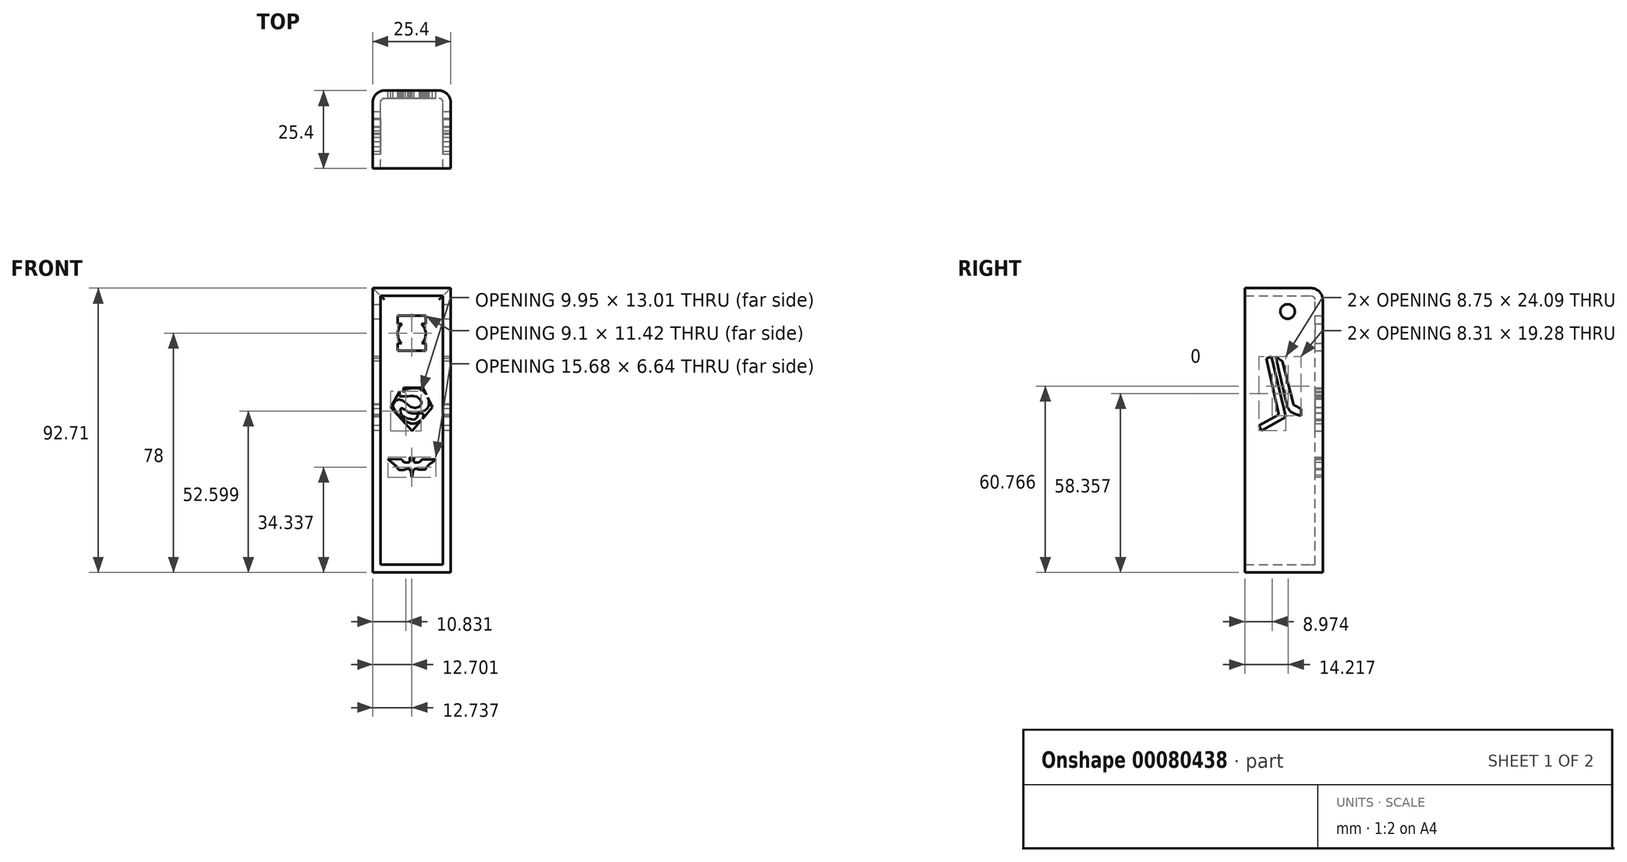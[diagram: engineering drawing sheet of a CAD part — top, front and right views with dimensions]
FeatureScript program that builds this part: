
annotation { "Feature Type Name" : "Feature", "Feature Type Description" : "" }
export const myFeature = defineFeature(function(context is Context, id is Id, definition is map)
    precondition{}
    {
        {
            var Q0;
            Q0=qCreatedBy(makeId("Front.planeOp"),FACE);
            var sketch = newSketch(context, id + "F0", { "sketchPlane" : qUnion([Q0])});
            skLineSegment(sketch, "E0.bottom", {"start": v(-54.67, 58.84) * mm, "end": v(-29.27, 58.84) * mm});
            skLineSegment(sketch, "E0.top", {"start": v(-54.67, -33.87) * mm, "end": v(-29.27, -33.87) * mm});
            skLineSegment(sketch, "E0.left", {"start": v(-54.67, 58.84) * mm, "end": v(-54.67, -33.87) * mm});
            skLineSegment(sketch, "E0.right", {"start": v(-29.27, 58.84) * mm, "end": v(-29.27, -33.87) * mm});
            skSolve(sketch);
        }
        {
            var Q0;
            Q0=makeQuery(id+"F0.imprint","IMPRINT",FACE,{"disambiguationData":[TD([[makeQuery(id+"F0.imprint","IMPRINT",EDGE,{"derivedFrom":sQuery(id+"F0.wireOp",EDGE,"E0.bottom")}),-1.0]])]});
            extrude(context, id + "F1", {"entities" : qUnion([Q0]), "depth" : 25.4 * mm});
        }
        {
            var Q0;
            Q0=makeQuery(id+"F1.opExtrude","CAP_EDGE",EDGE,{"disambiguationData":[OSD([sQuery(id+"F0.wireOp",EDGE,"E0.bottom")])],"isStart":true});
            var Q1;
            Q1=makeQuery(id+"F1.opExtrude","CAP_EDGE",EDGE,{"disambiguationData":[OSD([sQuery(id+"F0.wireOp",EDGE,"E0.right")])],"isStart":true});
            var Q2;
            Q2=makeQuery(id+"F1.opExtrude","CAP_EDGE",EDGE,{"disambiguationData":[OSD([sQuery(id+"F0.wireOp",EDGE,"E0.left")])],"isStart":true});
            fillet(context, id + "F2", {"entities" : qUnion([Q0, Q1, Q2]), "radius" : 3.8 * mm, "tangentPropagation" : true, "allowEdgeOverflow" : false});
        }
        {
            var Q0;
            Q0=makeQuery(id+"F1.opExtrude","CAP_FACE",FACE,{"disambiguationData":[OSD([sQuery(id+"F0.wireOp",EDGE,"E0.bottom"),sQuery(id+"F0.wireOp",EDGE,"E0.top"),sQuery(id+"F0.wireOp",EDGE,"E0.left"),sQuery(id+"F0.wireOp",EDGE,"E0.right")])],"isStart":false});
            shell(context, id + "F3", {"entities" : qUnion([Q0]), "thickness" : 2.54 * mm});
        }
        {
            var Q0;
            Q0=makeQuery(id+"F1.opExtrude","SWEPT_FACE",FACE,{"disambiguationData":[OSD([sQuery(id+"F0.wireOp",EDGE,"E0.right")])]});
            var sketch = newSketch(context, id + "F4", { "sketchPlane" : qUnion([Q0])});
            skCircle(sketch, "E1", {"center": v(-11.43, 51.22) * mm, "radius": 2.37 * mm});
            skSolve(sketch);
        }
        {
            var Q0;
            Q0=makeQuery(id+"F4.imprint","IMPRINT",FACE,{"disambiguationData":[TD([[makeQuery(id+"F4.imprint","IMPRINT",EDGE,{"derivedFrom":sQuery(id+"F4.wireOp",EDGE,"E1")}),1.0]])]});
            extrude(context, id + "F5", {"entities" : qUnion([Q0]), "operationType" : NewBodyOperationType.REMOVE, "oppositeDirection" : true, "depth" : 33.9 * mm});
        }
        {
            var Q0;
            Q0=makeQuery(id+"F1.opExtrude","CAP_FACE",FACE,{"disambiguationData":[OSD([sQuery(id+"F0.wireOp",EDGE,"E0.bottom"),sQuery(id+"F0.wireOp",EDGE,"E0.top"),sQuery(id+"F0.wireOp",EDGE,"E0.left"),sQuery(id+"F0.wireOp",EDGE,"E0.right")])],"isStart":true});
            var sketch = newSketch(context, id + "F6", { "sketchPlane" : qUnion([Q0])});
            skLineSegment(sketch, "E2", {"start": v(38.24, 26.3) * mm, "end": v(45.34, 26.3) * mm});
            skLineSegment(sketch, "E3", {"start": v(45.34, 26.3) * mm, "end": v(48.82, 20) * mm});
            skLineSegment(sketch, "E4", {"start": v(48.82, 20) * mm, "end": v(41.79, 12.22) * mm});
            skLineSegment(sketch, "E5", {"start": v(38.24, 26.3) * mm, "end": v(35.18, 20) * mm});
            skLineSegment(sketch, "E6", {"start": v(35.18, 20) * mm, "end": v(41.79, 12.22) * mm});
            skPoint(sketch, "E6.endSnap0", {"position": v(41.79, 26.3) * mm});
            skLineSegment(sketch, "E7", {"start": v(45.93, 25.23) * mm, "end": v(45.93, 23.52) * mm});
            skLineSegment(sketch, "E8", {"start": v(45.93, 23.52) * mm, "end": v(43.24, 23.52) * mm});
            skLineSegment(sketch, "E9", {"start": v(43.25, 18.52) * mm, "end": v(42.79, 18.26) * mm});
            skLineSegment(sketch, "E10", {"start": v(44.01, 25.93) * mm, "end": v(44.6, 24.83) * mm});
            skLineSegment(sketch, "E11", {"start": v(44.6, 24.83) * mm, "end": v(44.6, 26.3) * mm});
            skFitSpline(sketch, "E12", {"points": [v(43.24, 23.52) * mm, v(42.18, 23.7) * mm, v(41.34, 23.73) * mm, v(39, 22.4) * mm, v(38.86, 21.23) * mm, v(39.13, 20.53) * mm, v(40.91, 19.71) * mm, v(43.9, 21.34) * mm, v(46.12, 22.6) * mm, v(48.1, 20.99) * mm, v(47.19, 18.57) * mm, v(45.7, 16.78) * mm, v(42.61, 14.78) * mm, v(40.7, 14.7) * mm, v(38.86, 15.67) * mm, v(38.23, 16.65) * mm, v(38.36, 17.92) * mm, v(39.75, 17.72) * mm, v(40.62, 16.18) * mm, v(42.98, 16.28) * mm, v(45.43, 17.74) * mm, v(45.37, 19.7) * mm, v(42.79, 18.26) * mm, v(39.33, 18.25) * mm, v(36.88, 19.7) * mm, v(36.37, 21.85) * mm, v(37.82, 24.97) * mm, v(40.4, 26.27) * mm, v(44.01, 25.93) * mm], "startDerivative": vector(-64, 34.12) * mm, "endDerivative": vector(80.29, -7.6) * mm});
            skLineSegment(sketch, "E13", {"start": v(37.92, 26.85) * mm, "end": v(45.8, 26.85) * mm});
            skLineSegment(sketch, "E14", {"start": v(45.8, 26.85) * mm, "end": v(49.52, 20.02) * mm});
            skLineSegment(sketch, "E15", {"start": v(49.52, 20.02) * mm, "end": v(41.8, 11.45) * mm});
            skLineSegment(sketch, "E16", {"start": v(37.92, 26.85) * mm, "end": v(34.6, 20.06) * mm});
            skLineSegment(sketch, "E17", {"start": v(34.6, 20.06) * mm, "end": v(41.8, 11.45) * mm});
            skLineSegment(sketch, "E18", {"start": v(34.1, 3.04) * mm, "end": v(38.67, 3.04) * mm});
            skLineSegment(sketch, "E19", {"start": v(41.97, -31.17) * mm, "end": v(41.97, -31.17) * mm});
            skPoint(sketch, "E19.startSnap0", {"position": v(41.97, 55.03) * mm});
            skLineSegment(sketch, "E20", {"start": v(37.09, 0.46) * mm, "end": v(37.51, -0.37) * mm});
            skLineSegment(sketch, "E21", {"start": v(37.51, -0.37) * mm, "end": v(39.42, -0.37) * mm});
            skLineSegment(sketch, "E22.MirrorCS", {"start": v(49.77, 3.06) * mm, "end": v(45.2, 3.05) * mm});
            skFitSpline(sketch, "E23", {"points": [v(34.1, 3.04) * mm, v(37.09, 0.46) * mm, v(37.51, -0.37) * mm], "startDerivative": vector(5.4, -4.4) * mm, "endDerivative": vector(1.96, -3.42) * mm});
            skFitSpline(sketch, "E24", {"points": [v(37.51, -0.37) * mm, v(39.42, -0.37) * mm, v(41.5, -0.78) * mm, v(41.94, -2.12) * mm], "startDerivative": vector(3.85, 0) * mm, "endDerivative": vector(-0.02, 19.13) * mm});
            skFitSpline(sketch, "E25", {"points": [v(41.94, -2.12) * mm, v(42.38, -0.78) * mm, v(44.45, -0.37) * mm, v(46.36, -0.36) * mm], "startDerivative": vector(0.02, -19.13) * mm, "endDerivative": vector(4.94, -0.06) * mm});
            skFitSpline(sketch, "E26", {"points": [v(46.36, -0.36) * mm, v(46.78, 0.47) * mm, v(49.77, 3.06) * mm], "startDerivative": vector(1.36, 2.43) * mm, "endDerivative": vector(5.4, 4.4) * mm});
            skFitSpline(sketch, "E27", {"points": [v(45.2, 3.05) * mm, v(44.74, 2.33) * mm, v(43.56, 1.98) * mm, v(42.69, 2.24) * mm, v(42.69, 3.78) * mm], "startDerivative": vector(-2.36, -3.44) * mm, "endDerivative": vector(1.09, 6.4) * mm});
            skFitSpline(sketch, "E28", {"points": [v(41.18, 3.78) * mm, v(41.18, 2.24) * mm, v(40.3, 1.98) * mm, v(39.12, 2.32) * mm, v(38.67, 3.04) * mm], "startDerivative": vector(1.09, -6.4) * mm, "endDerivative": vector(-2.36, 3.44) * mm});
            skFitSpline(sketch, "E29", {"points": [v(41.18, 3.78) * mm, v(41.59, 3.12) * mm, v(41.93, 3.12) * mm, v(42.28, 3.12) * mm, v(42.69, 3.78) * mm], "startDerivative": vector(0.92, -3.28) * mm, "endDerivative": vector(0.92, 3.28) * mm});
            skPoint(sketch, "E30", {"position": v(37.3, 0.04) * mm});
            skLineSegment(sketch, "E31", {"start": v(41.97, 49.84) * mm, "end": v(37.42, 49.84) * mm});
            skLineSegment(sketch, "E32", {"start": v(37.42, 49.84) * mm, "end": v(37.42, 47.19) * mm});
            skLineSegment(sketch, "E33", {"start": v(37.42, 47.19) * mm, "end": v(40.3, 47.19) * mm});
            skLineSegment(sketch, "E34", {"start": v(40.3, 40.84) * mm, "end": v(37.42, 40.84) * mm});
            skLineSegment(sketch, "E35", {"start": v(37.42, 40.84) * mm, "end": v(37.42, 38.42) * mm});
            skLineSegment(sketch, "E36", {"start": v(37.42, 38.42) * mm, "end": v(41.97, 38.42) * mm});
            skCircle(sketch, "E37", {"center": v(41.97, 43.92) * mm, "radius": 4.55 * mm});
            skLineSegment(sketch, "E38", {"start": v(41.97, 49.84) * mm, "end": v(41.97, 38.42) * mm});
            skLineSegment(sketch, "E39.MirrorCS", {"start": v(46.52, 49.84) * mm, "end": v(46.52, 47.19) * mm});
            skLineSegment(sketch, "E40.MirrorCS", {"start": v(41.97, 49.84) * mm, "end": v(46.52, 49.84) * mm});
            skLineSegment(sketch, "E41.MirrorCS", {"start": v(46.52, 47.19) * mm, "end": v(43.64, 47.19) * mm});
            skLineSegment(sketch, "E42.MirrorCS", {"start": v(43.64, 40.84) * mm, "end": v(46.52, 40.84) * mm});
            skLineSegment(sketch, "E43.MirrorCS", {"start": v(46.52, 38.42) * mm, "end": v(41.97, 38.42) * mm});
            skLineSegment(sketch, "E44.MirrorCS", {"start": v(46.52, 40.84) * mm, "end": v(46.52, 38.42) * mm});
            skSolve(sketch);
        }
        {
            var Q0;
            {var subQ0=sQuery(id+"F6.wireOp",EDGE,"E19");var subQ1=sQuery(id+"F6.wireOp",EDGE,"E12");var subQ2=makeQuery(id+"F6.imprint","INTERSECT",VERTEX,{"disambiguationData":[OD(0.0)],"derivedFrom":[subQ1,subQ0]});Q0=makeQuery(id+"F6.imprint","IMPRINT",FACE,{"disambiguationData":[TD([[makeQuery(id+"F6.imprint","IMPRINT",EDGE,{"disambiguationData":[TD([[subQ2,-1.0]])],"derivedFrom":subQ1}),1.0]])]});}
            var Q1;
            {var subQ1=sQuery(id+"F6.wireOp",EDGE,"E5");var subQ5=sQuery(id+"F6.wireOp",EDGE,"E6");var subQ8=makeQuery(id+"F6.imprint","INTERSECT",VERTEX,{"derivedFrom":[subQ1,subQ5]});Q1=makeQuery(id+"F6.imprint","IMPRINT",FACE,{"disambiguationData":[TD([[makeQuery(id+"F6.imprint","IMPRINT",EDGE,{"disambiguationData":[TD([[subQ8,1.0]])],"derivedFrom":subQ1}),1.0]])]});}
            var Q2;
            {var subQ0=sQuery(id+"F6.wireOp",EDGE,"E5");var subQ1=sQuery(id+"F6.wireOp",EDGE,"E2");var subQ2=makeQuery(id+"F6.imprint","INTERSECT",VERTEX,{"derivedFrom":[subQ1,subQ0]});Q2=makeQuery(id+"F6.imprint","IMPRINT",FACE,{"disambiguationData":[TD([[makeQuery(id+"F6.imprint","IMPRINT",EDGE,{"disambiguationData":[TD([[subQ2,-1.0]])],"derivedFrom":subQ1}),-1.0]])]});}
            var Q3;
            {var subQ1=sQuery(id+"F6.wireOp",EDGE,"E10");Q3=makeQuery(id+"F6.imprint","IMPRINT",FACE,{"disambiguationData":[TD([[makeQuery(id+"F6.imprint","IMPRINT",EDGE,{"derivedFrom":subQ1}),1.0]])]});}
            var Q4;
            Q4=makeQuery(id+"F6.imprint","IMPRINT",FACE,{"disambiguationData":[TD([[makeQuery(id+"F6.imprint","IMPRINT",EDGE,{"derivedFrom":sQuery(id+"F6.wireOp",EDGE,"E22.MirrorCS")}),1.0]])]});
            var Q5;
            Q5=makeQuery(id+"F6.imprint","IMPRINT",FACE,{"disambiguationData":[TD([[makeQuery(id+"F6.imprint","IMPRINT",EDGE,{"derivedFrom":sQuery(id+"F6.wireOp",EDGE,"E18")}),-1.0]])]});
            var Q6;
            {var subQ5=sQuery(id+"F6.wireOp",EDGE,"E4");Q6=makeQuery(id+"F6.imprint","IMPRINT",FACE,{"disambiguationData":[TD([[makeQuery(id+"F6.imprint","IMPRINT",EDGE,{"derivedFrom":subQ5}),-1.0]])]});}
            var Q7;
            {var subQ4=sQuery(id+"F6.wireOp",EDGE,"E43.MirrorCS");Q7=makeQuery(id+"F6.imprint","IMPRINT",FACE,{"disambiguationData":[TD([[makeQuery(id+"F6.imprint","IMPRINT",EDGE,{"derivedFrom":subQ4}),-1.0]])]});}
            var Q8;
            {var subQ6=sQuery(id+"F6.wireOp",EDGE,"E35");Q8=makeQuery(id+"F6.imprint","IMPRINT",FACE,{"disambiguationData":[TD([[makeQuery(id+"F6.imprint","IMPRINT",EDGE,{"derivedFrom":subQ6}),1.0]])]});}
            var Q9;
            {var subQ0=sQuery(id+"F6.wireOp",EDGE,"E37");var subQ1=makeQuery(id+"F6.imprint","INTERSECT",VERTEX,{"derivedFrom":[sQuery(id+"F6.wireOp",EDGE,"E33"),subQ0]});Q9=makeQuery(id+"F6.imprint","IMPRINT",FACE,{"disambiguationData":[TD([[makeQuery(id+"F6.imprint","IMPRINT",EDGE,{"disambiguationData":[TD([[subQ1,1.0]])],"derivedFrom":subQ0}),1.0]])]});}
            var Q10;
            {var subQ0=sQuery(id+"F6.wireOp",EDGE,"E37");var subQ1=makeQuery(id+"F6.imprint","INTERSECT",VERTEX,{"derivedFrom":[subQ0,sQuery(id+"F6.wireOp",EDGE,"E41.MirrorCS")]});Q10=makeQuery(id+"F6.imprint","IMPRINT",FACE,{"disambiguationData":[TD([[makeQuery(id+"F6.imprint","IMPRINT",EDGE,{"disambiguationData":[TD([[subQ1,-1.0]])],"derivedFrom":subQ0}),1.0]])]});}
            var Q11;
            {var subQ1=sQuery(id+"F6.wireOp",EDGE,"E39.MirrorCS");Q11=makeQuery(id+"F6.imprint","IMPRINT",FACE,{"disambiguationData":[TD([[makeQuery(id+"F6.imprint","IMPRINT",EDGE,{"derivedFrom":subQ1}),-1.0]])]});}
            var Q12;
            {var subQ5=sQuery(id+"F6.wireOp",EDGE,"E31");Q12=makeQuery(id+"F6.imprint","IMPRINT",FACE,{"disambiguationData":[TD([[makeQuery(id+"F6.imprint","IMPRINT",EDGE,{"derivedFrom":subQ5}),1.0]])]});}
            extrude(context, id + "F7", {"entities" : qUnion([Q0, Q1, Q2, Q3, Q4, Q5, Q6, Q7, Q8, Q9, Q10, Q11, Q12]), "operationType" : NewBodyOperationType.REMOVE, "oppositeDirection" : true, "depth" : 25.4 * mm});
        }
        {
            var Q0;
            Q0=makeQuery(id+"F1.opExtrude","SWEPT_FACE",FACE,{"disambiguationData":[OSD([sQuery(id+"F0.wireOp",EDGE,"E0.left")])]});
            var sketch = newSketch(context, id + "F8", { "sketchPlane" : qUnion([Q0])});
            skLineSegment(sketch, "E45", {"start": v(15.34, 36.53) * mm, "end": v(11.77, 20.97) * mm});
            skFitSpline(sketch, "E46", {"points": [v(11.77, 20.97) * mm, v(10.36, 18.52) * mm, v(7.03, 17.26) * mm], "startDerivative": vector(-2.2, -5.88) * mm, "endDerivative": vector(-7.18, -1.63) * mm});
            skLineSegment(sketch, "E47", {"start": v(7.03, 17.26) * mm, "end": v(7.03, 19.52) * mm});
            skFitSpline(sketch, "E48", {"points": [v(7.03, 19.52) * mm, v(9.44, 20.8) * mm], "startDerivative": vector(2.42, 1.27) * mm, "endDerivative": vector(2.42, 1.27) * mm});
            skLineSegment(sketch, "E49", {"start": v(9.44, 20.8) * mm, "end": v(13.17, 35.04) * mm});
            skLineSegment(sketch, "E50", {"start": v(13.17, 35.04) * mm, "end": v(15.34, 36.53) * mm});
            skLineSegment(sketch, "E51", {"start": v(16.73, 36.53) * mm, "end": v(12.05, 16.8) * mm});
            skLineSegment(sketch, "E52", {"start": v(12.05, 16.8) * mm, "end": v(19.9, 12.44) * mm});
            skLineSegment(sketch, "E53", {"start": v(19.9, 12.44) * mm, "end": v(20.8, 14.05) * mm});
            skLineSegment(sketch, "E54", {"start": v(20.8, 14.05) * mm, "end": v(14.34, 17.64) * mm});
            skLineSegment(sketch, "E55", {"start": v(14.34, 17.64) * mm, "end": v(18.35, 35.9) * mm});
            skLineSegment(sketch, "E56", {"start": v(18.35, 35.9) * mm, "end": v(16.73, 36.53) * mm});
            skSolve(sketch);
        }
        {
            var Q0;
            Q0 = qSketchRegion(id + "F8", true);
            extrude(context, id + "F9", {"entities" : qUnion([Q0]), "operationType" : NewBodyOperationType.REMOVE, "oppositeDirection" : true, "depth" : 41.87 * mm});
        }
    });
